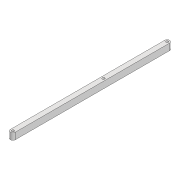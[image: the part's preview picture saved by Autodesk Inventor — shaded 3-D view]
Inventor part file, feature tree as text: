
AUTODESK INVENTOR PART (.ipt)
format: ipt  version: 2022 (Build 260153000, 153)  size: 89,088 bytes
history: native  units: mm
features: extrude x1, sketch x1
ambient origin geometry x8: Origin, YZ Plane, XZ Plane, XY Plane, X Axis, Y Axis, Z Axis, Center Point
bodies: Solid1 (feature_tree)
feature tree (2):
  extrude  "Extrusion1"  Depth=6.0mm
  sketch  "Sketch1"  dims[d0=189.323mm d1=6.0mm d2=3.0mm d3=3.0mm d4=8.0mm d5=0.0mm d6=3.0mm d7=111.208mm]
